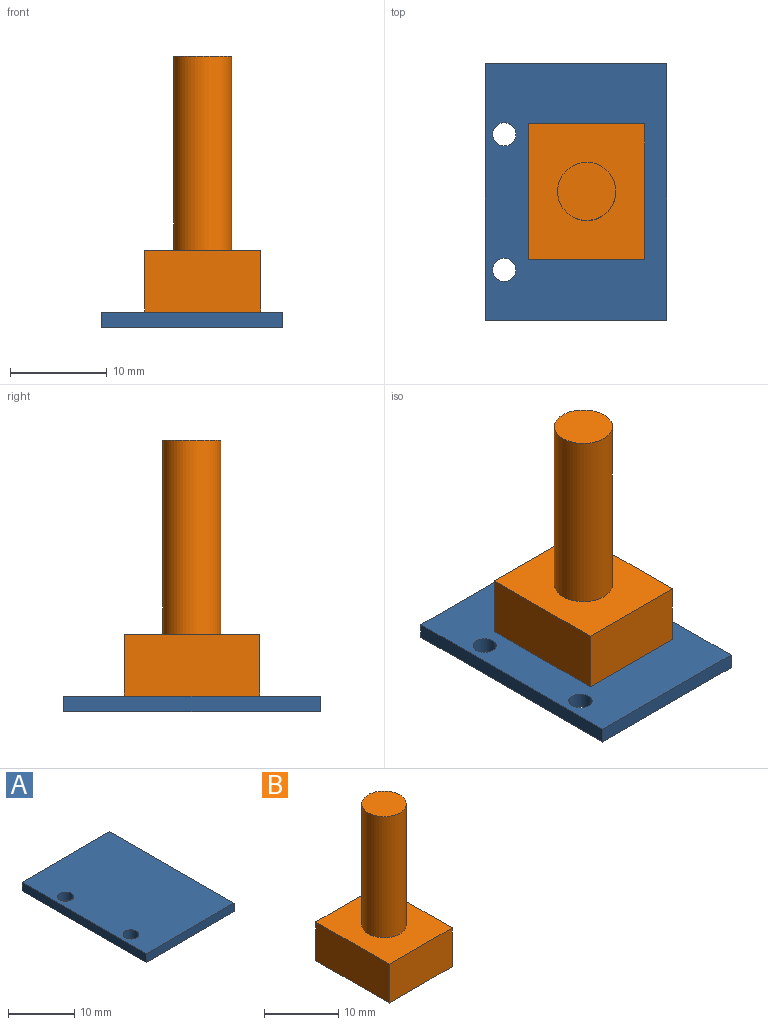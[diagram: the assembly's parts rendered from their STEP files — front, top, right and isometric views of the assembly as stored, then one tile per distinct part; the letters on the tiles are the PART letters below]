
ASSEMBLY  parts=2 mates=1
PART A: 8 faces, bbox 18.8x26.5x1.6 mm
  f0: plane 26.5x1.6mm, normal (1,0,0), area 42.4mm2, adj f1,f4,f6,f7
  f1: plane 18.8x1.6mm, normal (0,1,0), area 30.1mm2, adj f0,f2,f6,f7
  f2: plane 26.5x1.6mm, normal (-1,0,0), area 42.4mm2, adj f1,f4,f6,f7
  f3: cylinder r=1.2mm len=2.4mm, axis (0,0,-1), area 12.1mm2, adj f6,f7
  f4: plane 18.8x1.6mm, normal (0,-1,0), area 30.1mm2, adj f0,f2,f6,f7
  f5: cylinder r=1.2mm len=2.4mm, axis (0,0,-1), area 12.1mm2, adj f6,f7
  f6: plane 26.5x18.8mm, normal (0,0,1), area 489.2mm2, adj f0,f1,f2,f3,f4,f5
  f7: plane 26.5x18.8mm, normal (0,0,-1), area 489.2mm2, adj f0,f1,f2,f3,f4,f5
PART B: 8 faces, bbox 12x14x26.4 mm
  f0: plane 12x6.4mm, normal (0,1,0), area 76.8mm2, adj f1,f3,f4,f5
  f1: plane 14x6.4mm, normal (-1,0,0), area 89.6mm2, adj f0,f2,f4,f5
  f2: plane 12x6.4mm, normal (0,-1,0), area 76.8mm2, adj f1,f3,f4,f5
  f3: plane 14x6.4mm, normal (1,0,0), area 89.6mm2, adj f0,f2,f4,f5
  f4: plane 14x12mm, normal (0,0,1), area 139.7mm2, adj f0,f1,f2,f3,f6
  f5: plane 14x12mm, normal (0,0,-1), area 168mm2, adj f0,f1,f2,f3
  f6: cylinder r=3mm len=20mm, axis (0,0,-1), area 377mm2, adj f4,f7
  f7: plane 6x6mm, normal (0,0,1), area 28.3mm2, adj f6
PLACE A t=(0,-0.02,0)mm
PLACE B at identity
MATE fastened A.f6 <-> B.f5  axis (0,0,1) through (0.14,0,1.6)mm
